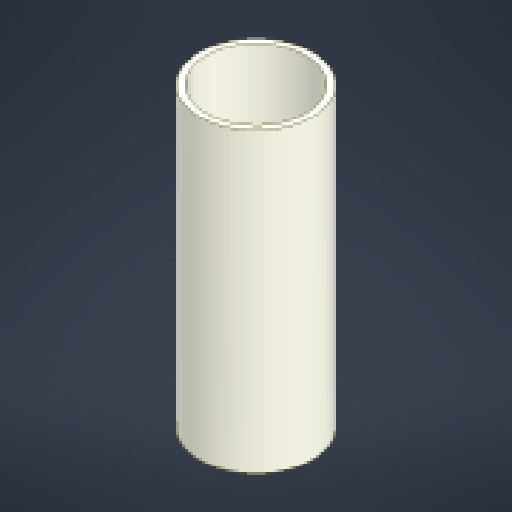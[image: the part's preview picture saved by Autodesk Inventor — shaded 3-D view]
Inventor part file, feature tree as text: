
AUTODESK INVENTOR PART (.ipt)
format: ipt  version: 2024.3 (Build 283343000, 343)  size: 109,056 bytes
history: native  units: in
note: dims shown in document units (in); Inventor stores cm internally (conversion verified against a paired STEP export)
features: extrude x1, sketch x1
ambient origin geometry x8: Origin, YZ Plane, XZ Plane, XY Plane, X Axis, Y Axis, Z Axis, Center Point
bodies: Solid1 (feature_tree)
feature tree (2):
  extrude  "Extrusion1"  Depth=11.875in
  sketch  "Sketch1"  dims[d0=4.5in d1=4.0in d2=11.875in d3=0.0in]
